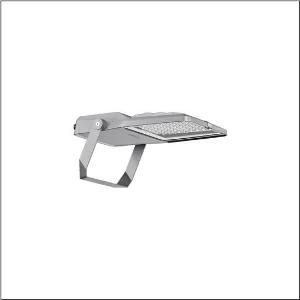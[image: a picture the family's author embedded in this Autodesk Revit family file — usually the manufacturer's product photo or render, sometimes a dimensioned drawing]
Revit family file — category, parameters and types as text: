
# Revit family: floodlight_fl_21_mini___pl64_5xa7775c2e1a_4676
name_source: partatom
category: Lighting Fixtures
units: mm (PartAtom-declared; Revit-internal decimal feet)

## family parameters
Cut with Voids When Loaded = No
Host = Face
Light Source = No
Part Type = Normal
Room Calculation Point = No
Round Connector Dimension = Use Diameter
Shared = No

## types (1)
- --- (1 x LED, 11770 lm, 89 W, 3000K)
    Apparent Load = 89 VA
    CIE Flux Codes = 28 80 98 100 100
    Color Rendering = 70
    Color Temperature = 3000K
    Default Elevation = 1800 mm
    Description = Floodlight FL 21 mini, floodlight, primary light control with lens, of PMMA, primary optical cover: protective disc, of toughened safety glass, transparent, light distribution: PL64, light emission: direct distribution, installation type: surface-mounted, LED, High Power LED, rated luminous flux: 11.770lm, luminous efficacy: 132lm/W, light colour: 730, colour temperature: 3000K, control gear: Smart Interface (Zhaga), control: flexible luminous flux parameterisation, time-dependent luminous flux control, constant luminous flux control, overheat protection, pre-setting: logarithmic dimming characteristic, with terminal, 6-pole, mains connection: 220..240V, AC, 50/60Hz, start of lifetime: 89W, end of service life: 94W, reduction: 43W, luminaire housing, of diecast aluminium, powder-coated, SITECO metallic grey (DB 702S), corrosivity category C5 mid according to DIN EN ISO 12944, suitable for swimming pools, chlorine-resistant, sealing non-destructively replaceable, mounting bracket, of steel, galvanised, powder-coated, SITECO metallic grey (DB 702S), Smart Interface above, protection rating (complete): IP66, insulation class (complete): insulation class II (safety insulation), certification: CE, ENEC, VDE, protection symbol: D, impact resistance: IK08, permissible operating ambient temperature: -40..+40°C, permissible operating ambient temperature for outdoor applications: -40..+50°C, standard: DIN EN 12944, LABS conformity tested according to VDMA 24364:2018-05, packaging unit: 1 piece

Light Distribution: PL64
    Height = 70 mm
    Lamp = 1 x LED
    Lamp Light Flux = 11770 lm
    Lamp Power = 89 W
    Lamp count = 1
    Length = 485 mm
    Luminous efficacy = 132 lm/W
    Manufacturer = Siteco
    ModVariant = No
    Model = 5XA7775C2E1A
    Mounting Place = Pole
    Mounting Type = Pole annexe
    Number of Poles = 1
    OnlyDefault = Yes
    Power Factor = 1
    Product Name = Floodlight FL 21 mini | PL64
    Product group = floodlight | pylon annexe
    ProductGroupID = 6201
    Protection Class = Protection class II
    Protection Degree = IP 66
    RLX_Detail_Level = 1
    RLX_Emergency_Light_Flux = 0 lm
    RLX_Emergency_Type = 0
    RLX_Emergency_Type_DB = No
    RlxData = <blob elided: 95945 chars, md5=cc8e3fee>
    Socket = socket
    Standby Power = 0 W
    System Light Flux = 11770 lm
    System Power = 89 W
    Type Comments = factory setting: luminous flux: 100 % | dim-lin: 254 | 456 mA
    Type Image = l_1006845.jpg
    URL = http://relux.com
    VarID = @adj_166475
    Voltage = 0 V
    Weight = 0.00 kg
    Width = 337 mm

## geometry (parser evidence)
native form markers: Blend x4, Sweep x13
no freeform markers — native parametric forms only
